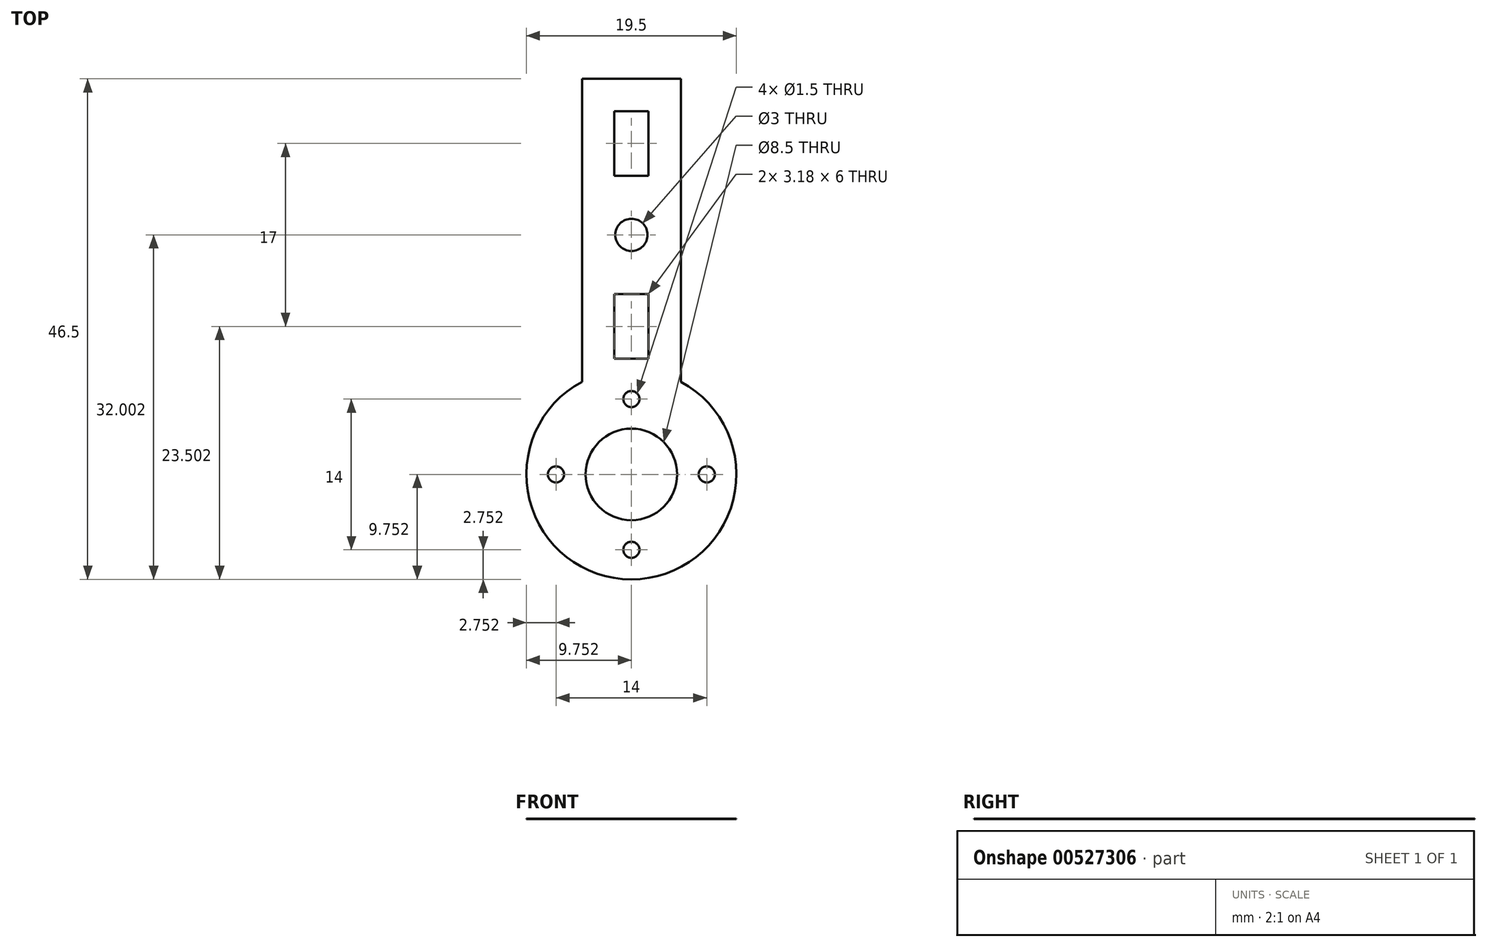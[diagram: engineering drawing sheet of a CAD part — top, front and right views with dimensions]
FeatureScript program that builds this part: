
annotation { "Feature Type Name" : "Feature", "Feature Type Description" : "" }
export const myFeature = defineFeature(function(context is Context, id is Id, definition is map)
    precondition{}
    {
        {
            var Q0;
            Q0=qCreatedBy(makeId("Top.planeOp"),FACE);
            var sketch = newSketch(context, id + "F0", { "sketchPlane" : qUnion([Q0])});
            skCircle(sketch, "E0", {"center": v(-20.73, 18.24) * mm, "radius": 0.75 * mm});
            skLineSegment(sketch, "E1", {"start": v(-23.6, 11.24) * mm, "end": v(-17.72, 11.24) * mm});
            skLineSegment(sketch, "E2", {"start": v(-20.73, 12.03) * mm, "end": v(-20.73, 6.8) * mm});
            skCircle(sketch, "E3.1.0", {"center": v(-27.73, 11.24) * mm, "radius": 0.75 * mm});
            skCircle(sketch, "E3.2.0", {"center": v(-20.73, 4.24) * mm, "radius": 0.75 * mm});
            skCircle(sketch, "E3.3.0", {"center": v(-13.73, 11.24) * mm, "radius": 0.75 * mm});
            skPoint(sketch, "E3.center", {"position": v(-20.73, 11.24) * mm});
            skCircle(sketch, "E4", {"center": v(-20.73, 11.24) * mm, "radius": 9.75 * mm});
            skCircle(sketch, "E5", {"center": v(-20.73, 11.24) * mm, "radius": 4.25 * mm});
            skCircle(sketch, "E6", {"center": v(-20.73, 33.5) * mm, "radius": 1.5 * mm});
            skLineSegment(sketch, "E7.bottom", {"start": v(-22.32, 28) * mm, "end": v(-19.14, 28) * mm});
            skLineSegment(sketch, "E7.top", {"start": v(-22.32, 22) * mm, "end": v(-19.14, 22) * mm});
            skLineSegment(sketch, "E7.left", {"start": v(-22.32, 28) * mm, "end": v(-22.32, 22) * mm});
            skLineSegment(sketch, "E7.right", {"start": v(-19.14, 28) * mm, "end": v(-19.14, 22) * mm});
            skPoint(sketch, "E7.middle", {"position": v(-20.73, 25) * mm});
            skLineSegment(sketch, "E8", {"start": v(-20.73, 33.5) * mm, "end": v(-22.23, 33.5) * mm});
            skLineSegment(sketch, "E9.MirrorCS", {"start": v(-22.32, 39) * mm, "end": v(-19.14, 39) * mm});
            skLineSegment(sketch, "E10.MirrorCS", {"start": v(-22.32, 39) * mm, "end": v(-22.32, 45) * mm});
            skLineSegment(sketch, "E11.MirrorCS", {"start": v(-19.14, 39) * mm, "end": v(-19.14, 45) * mm});
            skLineSegment(sketch, "E12.MirrorCS", {"start": v(-22.32, 45) * mm, "end": v(-19.14, 45) * mm});
            skLineSegment(sketch, "E13.bottom", {"start": v(-25.32, 48) * mm, "end": v(-16.14, 48) * mm});
            skLineSegment(sketch, "E13.left", {"start": v(-25.32, 48) * mm, "end": v(-25.32, 19.85) * mm});
            skLineSegment(sketch, "E13.right", {"start": v(-16.14, 48) * mm, "end": v(-16.14, 19.85) * mm});
            skSolve(sketch);
        }
        {
            var Q0;
            Q0=makeQuery(id+"F0.imprint","IMPRINT",FACE,{"disambiguationData":[TD([[makeQuery(id+"F0.imprint","IMPRINT",EDGE,{"derivedFrom":sQuery(id+"F0.wireOp",EDGE,"E6")}),-1.0]])]});
            var Q1;
            Q1=makeQuery(id+"F0.imprint","IMPRINT",FACE,{"disambiguationData":[TD([[makeQuery(id+"F0.imprint","IMPRINT",EDGE,{"derivedFrom":sQuery(id+"F0.wireOp",EDGE,"E0")}),-1.0]])]});
            extrude(context, id + "F1", {"entities" : qUnion([Q0, Q1]), "depth" : 1 / 203.2 * mm, "offsetDistance" : 25 * mm});
        }
    });
